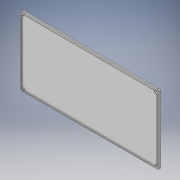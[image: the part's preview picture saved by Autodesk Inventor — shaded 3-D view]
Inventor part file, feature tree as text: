
AUTODESK INVENTOR PART (.ipt)
format: ipt  version: 2019.4 (Build 234330000, 330)  size: 209,408 bytes
history: native  units: mm
features: extrude x3, sketch x1
ambient origin geometry x8: Origin, YZ Plane, XZ Plane, XY Plane, X Axis, Y Axis, Z Axis, Center Point
bodies: Solid1 (feature_tree)
feature tree (4):
  sketch  "Sketch1"  dims[d0=300.0mm d1=150.0mm d2=295.0mm d3=145.0mm d4=4.0mm d5=4.0mm d6=4.0mm d7=4.0mm d8=4.0mm d9=4.0mm d10=4.0mm d11=4.0mm d12=4.0mm d13=4.0mm d14=4.0mm d15=4.0mm d16=5.0mm d17=5.0mm d18=5.0mm d19=5.0mm d20=4.0mm d21=4.0mm d22=4.0mm d23=4.0mm d24=4.0mm d25=4.0mm d26=4.0mm d27=4.0mm d28=4.0mm d29=4.0mm d30=4.0mm d31=4.0mm d32=1.5mm d33=1.5mm d34=1.5mm d35=1.5mm d36=1.5mm d37=1.5mm d38=1.5mm d39=1.5mm d40=1.5mm d41=1.5mm d42=1.5mm d43=1.5mm d44=1.5mm d45=1.5mm d46=1.5mm d47=1.5mm d48=1.5mm d49=1.5mm d50=1.5mm d51=1.5mm d52=1.5mm d53=1.5mm d54=1.5mm d55=1.5mm d56=2.5mm d57=0.0mm d58=0.5mm d59=0.0mm d60=9.5mm d61=9.5mm d62=140.5mm d63=290.5mm d64=5.0mm d65=0.0mm]
  extrude  "Extrusion1"  Depth=2.5mm TaperAngle=0.0deg
  extrude  "Extrusion2"  Depth=0.5mm TaperAngle=0.0deg
  extrude  "Extrusion3"  Depth=5.0mm
